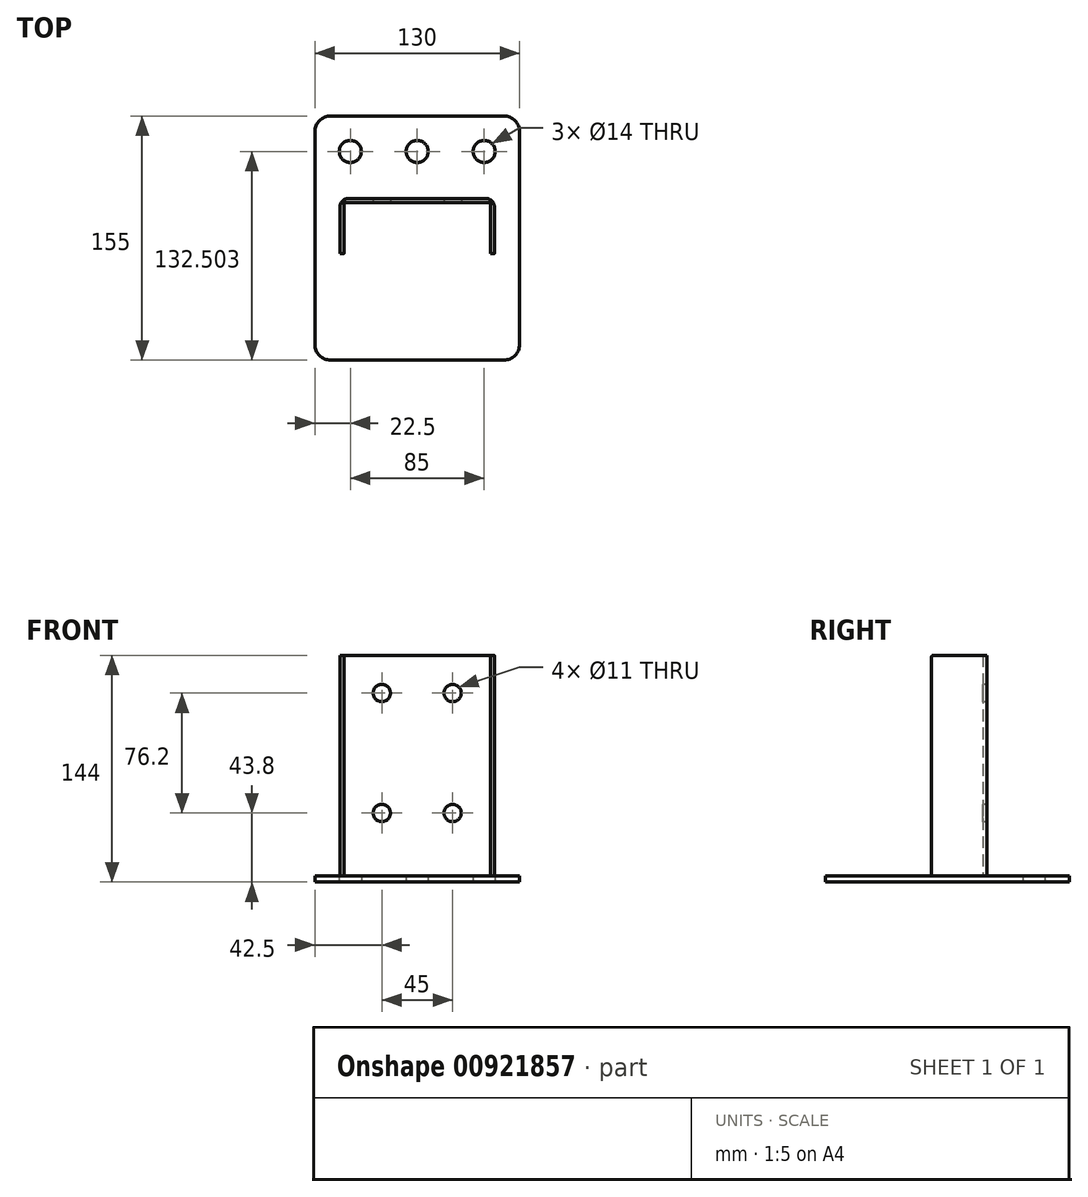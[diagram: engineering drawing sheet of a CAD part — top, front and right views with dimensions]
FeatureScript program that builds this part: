
annotation { "Feature Type Name" : "Feature", "Feature Type Description" : "" }
export const myFeature = defineFeature(function(context is Context, id is Id, definition is map)
    precondition{}
    {
        {
            var Q0;
            Q0=qCreatedBy(makeId("Top.planeOp"),FACE);
            var sketch = newSketch(context, id + "F0", { "sketchPlane" : qUnion([Q0])});
            skLineSegment(sketch, "E0.bottom", {"start": v(-130, -40.68) * mm, "end": v(0, -40.68) * mm});
            skLineSegment(sketch, "E0.top", {"start": v(-130, 114.32) * mm, "end": v(0, 114.32) * mm});
            skLineSegment(sketch, "E0.left", {"start": v(-130, -40.68) * mm, "end": v(-130, 114.32) * mm});
            skLineSegment(sketch, "E0.right", {"start": v(0, -40.68) * mm, "end": v(0, 114.32) * mm});
            skSolve(sketch);
        }
        {
            var Q0;
            Q0=makeQuery(id+"F0.imprint","IMPRINT",FACE,{"disambiguationData":[TD([[makeQuery(id+"F0.imprint","IMPRINT",EDGE,{"derivedFrom":sQuery(id+"F0.wireOp",EDGE,"E0.bottom")}),1.0]])]});
            extrude(context, id + "F1", {"entities" : qUnion([Q0]), "depth" : 4 * mm, "offsetDistance" : 25 * mm});
        }
        {
            var Q0;
            Q0=makeQuery(id+"F1.opExtrude","SWEPT_EDGE",EDGE,{"disambiguationData":[OSD([sQuery(id+"F0.wireOp",EDGE,"E0.bottom"),sQuery(id+"F0.wireOp",EDGE,"E0.right")])]});
            var Q1;
            Q1=makeQuery(id+"F1.opExtrude","SWEPT_EDGE",EDGE,{"disambiguationData":[OSD([sQuery(id+"F0.wireOp",EDGE,"E0.top"),sQuery(id+"F0.wireOp",EDGE,"E0.right")])]});
            var Q2;
            Q2=makeQuery(id+"F1.opExtrude","SWEPT_EDGE",EDGE,{"disambiguationData":[OSD([sQuery(id+"F0.wireOp",EDGE,"E0.top"),sQuery(id+"F0.wireOp",EDGE,"E0.left")])]});
            var Q3;
            Q3=makeQuery(id+"F1.opExtrude","SWEPT_EDGE",EDGE,{"disambiguationData":[OSD([sQuery(id+"F0.wireOp",EDGE,"E0.bottom"),sQuery(id+"F0.wireOp",EDGE,"E0.left")])]});
            fillet(context, id + "F2", {"entities" : qUnion([Q0, Q1, Q2, Q3]), "radius" : 10 * mm, "tangentPropagation" : true, "allowEdgeOverflow" : false});
        }
        {
            var Q0;
            Q0=makeQuery(id+"F1.opExtrude","CAP_FACE",FACE,{"disambiguationData":[OSD([sQuery(id+"F0.wireOp",EDGE,"E0.bottom"),sQuery(id+"F0.wireOp",EDGE,"E0.top"),sQuery(id+"F0.wireOp",EDGE,"E0.left"),sQuery(id+"F0.wireOp",EDGE,"E0.right")])],"isStart":false});
            var sketch = newSketch(context, id + "F3", { "sketchPlane" : qUnion([Q0])});
            skLineSegment(sketch, "E1", {"start": v(-16, 61.82) * mm, "end": v(-16, 26.82) * mm});
            skLineSegment(sketch, "E2", {"start": v(-16, 26.82) * mm, "end": v(-18.5, 26.82) * mm});
            skLineSegment(sketch, "E3", {"start": v(-18.5, 26.82) * mm, "end": v(-18.5, 59.32) * mm});
            skLineSegment(sketch, "E4", {"start": v(-18.5, 59.32) * mm, "end": v(-111.5, 59.32) * mm});
            skLineSegment(sketch, "E5", {"start": v(-111.5, 59.32) * mm, "end": v(-111.5, 26.82) * mm});
            skLineSegment(sketch, "E6", {"start": v(-111.5, 26.82) * mm, "end": v(-114, 26.82) * mm});
            skLineSegment(sketch, "E7", {"start": v(-114, 26.82) * mm, "end": v(-114, 61.82) * mm});
            skLineSegment(sketch, "E8", {"start": v(-16, 61.82) * mm, "end": v(-114, 61.82) * mm});
            skSolve(sketch);
        }
        {
            var Q0;
            Q0=makeQuery(id+"F3.imprint","IMPRINT",FACE,{"disambiguationData":[TD([[makeQuery(id+"F3.imprint","IMPRINT",EDGE,{"derivedFrom":sQuery(id+"F3.wireOp",EDGE,"E1")}),-1.0]])]});
            extrude(context, id + "F4", {"entities" : qUnion([Q0]), "operationType" : NewBodyOperationType.ADD, "depth" : 140 * mm, "offsetDistance" : 25 * mm});
        }
        {
            var Q0;
            Q0=makeQuery(id+"F4.opExtrude","SWEPT_EDGE",EDGE,{"disambiguationData":[OSD([sQuery(id+"F3.wireOp",EDGE,"E7"),sQuery(id+"F3.wireOp",EDGE,"E8")])]});
            var Q1;
            Q1=makeQuery(id+"F4.opExtrude","SWEPT_EDGE",EDGE,{"disambiguationData":[OSD([sQuery(id+"F3.wireOp",EDGE,"E1"),sQuery(id+"F3.wireOp",EDGE,"E8")])]});
            fillet(context, id + "F5", {"entities" : qUnion([Q0, Q1]), "radius" : 5 * mm, "tangentPropagation" : true, "allowEdgeOverflow" : false});
        }
        {
            var Q0;
            Q0=makeQuery(id+"F4.opExtrude","SWEPT_EDGE",EDGE,{"disambiguationData":[OSD([sQuery(id+"F3.wireOp",EDGE,"E3"),sQuery(id+"F3.wireOp",EDGE,"E4")])]});
            var Q1;
            Q1=makeQuery(id+"F4.opExtrude","SWEPT_EDGE",EDGE,{"disambiguationData":[OSD([sQuery(id+"F3.wireOp",EDGE,"E4"),sQuery(id+"F3.wireOp",EDGE,"E5")])]});
            fillet(context, id + "F6", {"entities" : qUnion([Q0, Q1]), "radius" : 1 * mm, "tangentPropagation" : true, "allowEdgeOverflow" : false});
        }
        {
            var Q0;
            Q0=makeQuery(id+"F4.opExtrude","CAP_EDGE",EDGE,{"disambiguationData":[OSD([sQuery(id+"F3.wireOp",EDGE,"E6")])],"isStart":false});
            var Q1;
            Q1=makeQuery(id+"F4.opExtrude","CAP_EDGE",EDGE,{"disambiguationData":[OSD([sQuery(id+"F3.wireOp",EDGE,"E2")])],"isStart":false});
            fillet(context, id + "F7", {"entities" : qUnion([Q0, Q1]), "radius" : 1 * mm, "tangentPropagation" : true, "allowEdgeOverflow" : false});
        }
        {
            var Q0;
            Q0=makeQuery(id+"F1.opExtrude","CAP_FACE",FACE,{"disambiguationData":[OSD([sQuery(id+"F0.wireOp",EDGE,"E0.bottom"),sQuery(id+"F0.wireOp",EDGE,"E0.top"),sQuery(id+"F0.wireOp",EDGE,"E0.left"),sQuery(id+"F0.wireOp",EDGE,"E0.right")])],"isStart":false});
            var sketch = newSketch(context, id + "F8", { "sketchPlane" : qUnion([Q0])});
            skCircle(sketch, "E9", {"center": v(-22.5, 91.82) * mm, "radius": 7.47 * mm});
            skCircle(sketch, "E10", {"center": v(-65, 91.82) * mm, "radius": 7.47 * mm});
            skCircle(sketch, "E11", {"center": v(-107.5, 91.82) * mm, "radius": 7.47 * mm});
            skSolve(sketch);
        }
        {
            var Q0;
            Q0=sQuery(id+"F8.wireOp",VERTEX,"E9.center");
            var Q1;
            Q1=sQuery(id+"F8.wireOp",VERTEX,"E10.center");
            var Q2;
            Q2=sQuery(id+"F8.wireOp",VERTEX,"E11.center");
            var Q3;
            Q3=makeQuery(id+"F1.opExtrude","SWEPT_BODY",BODY,{"disambiguationData":[OSD([sQuery(id+"F0.wireOp",EDGE,"E0.bottom"),sQuery(id+"F0.wireOp",EDGE,"E0.top"),sQuery(id+"F0.wireOp",EDGE,"E0.left"),sQuery(id+"F0.wireOp",EDGE,"E0.right")])]});
            hole(context, id + "F9", {"style" : HoleStyle.SIMPLE, "endStyle" : HoleEndStyle.THROUGH, "holeDiameter" : 14 * mm, "majorDiameter" : 5 * mm, "isTappedThrough" : true, "tappedDepth" : 12 * mm, "tapClearance" : 3, "locations" : qUnion([Q0, Q1, Q2]), "scope" : qUnion([Q3]), "startStyle" : HoleStartStyle.PART});
        }
        {
            var Q0;
            Q0=makeQuery(id+"F4.opExtrude","SWEPT_FACE",FACE,{"disambiguationData":[OSD([sQuery(id+"F3.wireOp",EDGE,"E8")])]});
            var sketch = newSketch(context, id + "F10", { "sketchPlane" : qUnion([Q0])});
            skCircle(sketch, "E12", {"center": v(42.5, 120) * mm, "radius": 5.5 * mm});
            skCircle(sketch, "E13.0.1.0", {"center": v(42.5, 43.8) * mm, "radius": 5.5 * mm});
            skCircle(sketch, "E13.1.0.0", {"center": v(87.5, 120) * mm, "radius": 5.5 * mm});
            skCircle(sketch, "E13.1.1.0", {"center": v(87.5, 43.8) * mm, "radius": 5.5 * mm});
            skLineSegment(sketch, "E13.direction2", {"start": v(42.5, 120) * mm, "end": v(42.5, 43.8) * mm, "construction": true});
            skSolve(sketch);
        }
        {
            var Q0;
            Q0=sQuery(id+"F10.wireOp",VERTEX,"E13.direction1.end");
            var Q1;
            Q1=sQuery(id+"F10.wireOp",VERTEX,"E13.direction1.start");
            var Q2;
            Q2=sQuery(id+"F10.wireOp",VERTEX,"E13.direction2.end");
            var Q3;
            Q3=sQuery(id+"F10.wireOp",VERTEX,"E13.1.1.0.center");
            var Q4;
            Q4=sQuery(id+"F10.wireOp",VERTEX,"E13.direction2.start");
            var Q5;
            Q5=sQuery(id+"F10.wireOp",VERTEX,"E13.1.0.0.center");
            var Q6;
            Q6=makeQuery(id+"F1.opExtrude","SWEPT_BODY",BODY,{"disambiguationData":[OSD([sQuery(id+"F0.wireOp",EDGE,"E0.bottom"),sQuery(id+"F0.wireOp",EDGE,"E0.top"),sQuery(id+"F0.wireOp",EDGE,"E0.left"),sQuery(id+"F0.wireOp",EDGE,"E0.right")])]});
            hole(context, id + "F11", {"style" : HoleStyle.SIMPLE, "endStyle" : HoleEndStyle.THROUGH, "holeDiameter" : 11 * mm, "majorDiameter" : 5 * mm, "isTappedThrough" : true, "tappedDepth" : 12 * mm, "tapClearance" : 3, "locations" : qUnion([Q0, Q1, Q2, Q3, Q4, Q5]), "scope" : qUnion([Q6]), "startStyle" : HoleStartStyle.PART});
        }
    });
